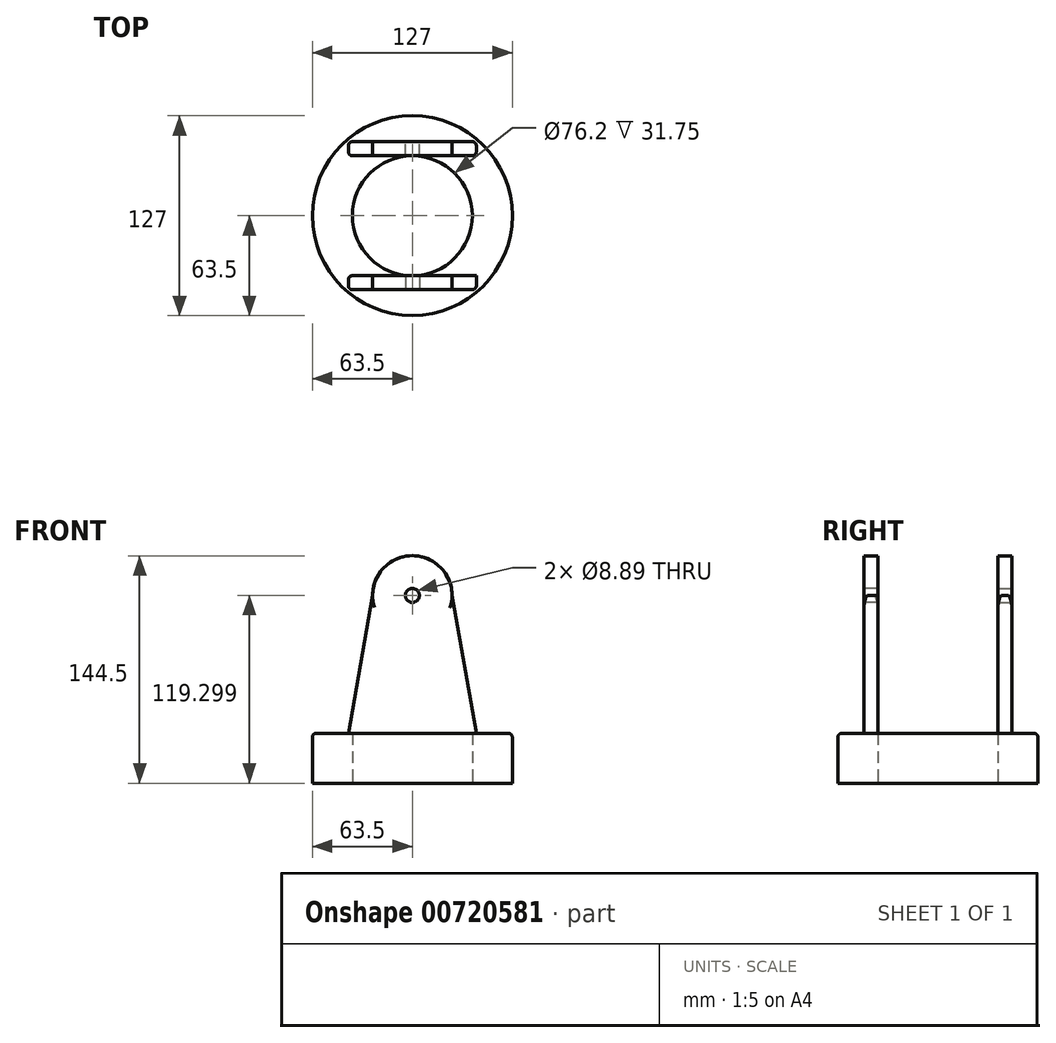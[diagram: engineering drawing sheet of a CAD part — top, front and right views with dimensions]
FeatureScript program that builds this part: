
annotation { "Feature Type Name" : "Feature", "Feature Type Description" : "" }
export const myFeature = defineFeature(function(context is Context, id is Id, definition is map)
    precondition{}
    {
        {
            var Q0;
            Q0=qCreatedBy(makeId("Top.planeOp"),FACE);
            var sketch = newSketch(context, id + "F0", { "sketchPlane" : qUnion([Q0])});
            skCircle(sketch, "E0", {"center": v(0, 0) * mm, "radius": 63.5 * mm});
            skCircle(sketch, "E1", {"center": v(0, 0) * mm, "radius": 38.1 * mm});
            skSolve(sketch);
        }
        {
            var Q0;
            Q0=makeQuery(id+"F0.imprint","IMPRINT",FACE,{"disambiguationData":[TD([[makeQuery(id+"F0.imprint","IMPRINT",EDGE,{"derivedFrom":sQuery(id+"F0.wireOp",EDGE,"E0")}),1.0]])]});
            extrude(context, id + "F1", {"entities" : qUnion([Q0]), "depth" : 31.75 * mm, "offsetDistance" : 25.4 * mm});
        }
        {
            var Q0;
            Q0=qCreatedBy(makeId("Front.planeOp"),FACE);
            cPlane(context, id + "F2", {"entities" : qUnion([Q0]), "cplaneType" : CPlaneType.OFFSET, "offset" : 38.1 * mm, "width" : 152.4 * mm, "height" : 152.4 * mm});
        }
        {
            var Q0;
            Q0=qCreatedBy(id+"F2.planeOp",FACE);
            var sketch = newSketch(context, id + "F3", { "sketchPlane" : qUnion([Q0])});
            skLineSegment(sketch, "E2", {"start": v(-40.64, 31.75) * mm, "end": v(40.64, 31.75) * mm});
            skLineSegment(sketch, "E3", {"start": v(-40.64, 31.75) * mm, "end": v(-25.2, 119.3) * mm});
            skLineSegment(sketch, "E4", {"start": v(40.64, 31.75) * mm, "end": v(25.2, 119.3) * mm});
            skArc(sketch, "E5", {"start": v(25.2, 119.3) * mm, "mid": v(0, 144.5) * mm, "end": v(-25.2, 119.3) * mm});
            skSolve(sketch);
        }
        {
            var Q0;
            Q0=makeQuery(id+"F3.imprint","IMPRINT",FACE,{"disambiguationData":[TD([[makeQuery(id+"F3.imprint","IMPRINT",EDGE,{"derivedFrom":sQuery(id+"F3.wireOp",EDGE,"E2")}),1.0]])]});
            extrude(context, id + "F4", {"entities" : qUnion([Q0]), "operationType" : NewBodyOperationType.ADD, "depth" : 8.9 * mm, "offsetDistance" : 25.4 * mm});
        }
        {
            var Q0;
            Q0=qCreatedBy(makeId("Front.planeOp"),FACE);
            cPlane(context, id + "F5", {"entities" : qUnion([Q0]), "cplaneType" : CPlaneType.OFFSET, "offset" : 38.1 * mm, "oppositeDirection" : true, "width" : 152.4 * mm, "height" : 152.4 * mm});
        }
        {
            var Q0;
            Q0=qCreatedBy(id+"F5.planeOp",FACE);
            var sketch = newSketch(context, id + "F6", { "sketchPlane" : qUnion([Q0])});
            skLineSegment(sketch, "E6", {"start": v(-40.64, 31.75) * mm, "end": v(-25.2, 119.3) * mm});
            skLineSegment(sketch, "E7", {"start": v(40.64, 31.75) * mm, "end": v(25.2, 119.3) * mm});
            skArc(sketch, "E8", {"start": v(25.2, 119.3) * mm, "mid": v(0, 144.5) * mm, "end": v(-25.2, 119.3) * mm});
            skLineSegment(sketch, "E9", {"start": v(40.64, 31.75) * mm, "end": v(-40.64, 31.75) * mm});
            skSolve(sketch);
        }
        {
            var Q0;
            Q0=makeQuery(id+"F1.opExtrude","CAP_EDGE",EDGE,{"disambiguationData":[OSD([sQuery(id+"F0.wireOp",EDGE,"E0")])],"isStart":false});
            fillet(context, id + "F7", {"entities" : qUnion([Q0]), "radius" : 2.54 * mm, "tangentPropagation" : true, "allowEdgeOverflow" : false});
        }
        {
            var Q0;
            Q0=makeQuery(id+"F4.opExtrude","CAP_FACE",FACE,{"disambiguationData":[OSD([sQuery(id+"F3.wireOp",EDGE,"E2"),sQuery(id+"F3.wireOp",EDGE,"E3"),sQuery(id+"F3.wireOp",EDGE,"E4"),sQuery(id+"F3.wireOp",EDGE,"E5")])],"isStart":false});
            var sketch = newSketch(context, id + "F8", { "sketchPlane" : qUnion([Q0])});
            skPoint(sketch, "E10", {"position": v(0, 119.3) * mm});
            skSolve(sketch);
        }
        {
            var Q0;
            Q0=sQuery(id+"F8.wireOp",VERTEX,"E10");
            var Q1;
            Q1=makeQuery(id+"F1.opExtrude","SWEPT_BODY",BODY,{"disambiguationData":[OSD([sQuery(id+"F0.wireOp",EDGE,"E0"),sQuery(id+"F0.wireOp",EDGE,"E1")])]});
            hole(context, id + "F9", {"style" : HoleStyle.SIMPLE, "endStyle" : HoleEndStyle.THROUGH, "holeDiameter" : 8.9 * mm, "majorDiameter" : 6.35 * mm, "isTappedThrough" : true, "tappedDepth" : 12.7 * mm, "tapClearance" : 3, "startFromSketch" : true, "locations" : qUnion([Q0]), "scope" : qUnion([Q1])});
        }
        {
            var Q0;
            Q0=makeQuery(id+"F4.opExtrude","CAP_EDGE",EDGE,{"disambiguationData":[OSD([sQuery(id+"F3.wireOp",EDGE,"E4")])],"isStart":false});
            var Q1;
            Q1=makeQuery(id+"FsUpcKdfloYsDhg_1.opExtrude","CAP_EDGE",EDGE,{"disambiguationData":[OSD([sQuery(id+"F6.wireOp",EDGE,"E7")])],"isStart":true});
            var Q2;
            Q2=makeQuery(id+"FsUpcKdfloYsDhg_1.opExtrude","CAP_EDGE",EDGE,{"disambiguationData":[OSD([sQuery(id+"F6.wireOp",EDGE,"E7")])],"isStart":false});
            var Q3;
            Q3=makeQuery(id+"F4.opExtrude","CAP_EDGE",EDGE,{"disambiguationData":[OSD([sQuery(id+"F3.wireOp",EDGE,"E3")])],"isStart":false});
            var Q4;
            Q4=makeQuery(id+"F4.opExtrude","CAP_EDGE",EDGE,{"disambiguationData":[OSD([sQuery(id+"F3.wireOp",EDGE,"E3")])],"isStart":true});
            var Q5;
            Q5=makeQuery(id+"FsUpcKdfloYsDhg_1.opExtrude","CAP_EDGE",EDGE,{"disambiguationData":[OSD([sQuery(id+"F6.wireOp",EDGE,"E6")])],"isStart":true});
            fillet(context, id + "F10", {"entities" : qUnion([Q0, Q1, Q2, Q3, Q4, Q5]), "radius" : 2.54 * mm, "tangentPropagation" : true, "allowEdgeOverflow" : false});
        }
        {
            var Q0;
            Q0=makeQuery(id+"F6.imprint","IMPRINT",FACE,{"disambiguationData":[TD([[makeQuery(id+"F6.imprint","IMPRINT",EDGE,{"derivedFrom":sQuery(id+"F6.wireOp",EDGE,"E6")}),-1.0]])]});
            extrude(context, id + "F11", {"entities" : qUnion([Q0]), "operationType" : NewBodyOperationType.ADD, "oppositeDirection" : true, "depth" : 8.9 * mm, "offsetDistance" : 25.4 * mm});
        }
        {
            var Q0;
            Q0=makeQuery(id+"F11.opExtrude","CAP_FACE",FACE,{"disambiguationData":[OSD([sQuery(id+"F6.wireOp",EDGE,"E6"),sQuery(id+"F6.wireOp",EDGE,"E7"),sQuery(id+"F6.wireOp",EDGE,"E8"),sQuery(id+"F6.wireOp",EDGE,"E9")])],"isStart":false});
            var sketch = newSketch(context, id + "F12", { "sketchPlane" : qUnion([Q0])});
            skPoint(sketch, "E11", {"position": v(0, 119.3) * mm});
            skSolve(sketch);
        }
        {
            var Q0;
            Q0=sQuery(id+"F12.wireOp",VERTEX,"E11");
            var Q1;
            Q1=makeQuery(id+"F1.opExtrude","SWEPT_BODY",BODY,{"disambiguationData":[OSD([sQuery(id+"F0.wireOp",EDGE,"E0"),sQuery(id+"F0.wireOp",EDGE,"E1")])]});
            hole(context, id + "F13", {"style" : HoleStyle.SIMPLE, "endStyle" : HoleEndStyle.THROUGH, "holeDiameter" : 8.9 * mm, "majorDiameter" : 6.35 * mm, "isTappedThrough" : true, "tappedDepth" : 12.7 * mm, "tapClearance" : 3, "startFromSketch" : true, "locations" : qUnion([Q0]), "scope" : qUnion([Q1])});
        }
        {
            var Q0;
            Q0=makeQuery(id+"F11.opExtrude","CAP_EDGE",EDGE,{"disambiguationData":[OSD([sQuery(id+"F6.wireOp",EDGE,"E7")])],"isStart":true});
            var Q1;
            Q1=makeQuery(id+"F11.opExtrude","CAP_EDGE",EDGE,{"disambiguationData":[OSD([sQuery(id+"F6.wireOp",EDGE,"E7")])],"isStart":false});
            var Q2;
            Q2=makeQuery(id+"F11.opExtrude","CAP_EDGE",EDGE,{"disambiguationData":[OSD([sQuery(id+"F6.wireOp",EDGE,"E6")])],"isStart":true});
            var Q3;
            Q3=makeQuery(id+"F11.opExtrude","CAP_EDGE",EDGE,{"disambiguationData":[OSD([sQuery(id+"F6.wireOp",EDGE,"E6")])],"isStart":false});
            fillet(context, id + "F14", {"entities" : qUnion([Q0, Q1, Q2, Q3]), "radius" : 2.54 * mm, "tangentPropagation" : true, "allowEdgeOverflow" : false});
        }
    });
